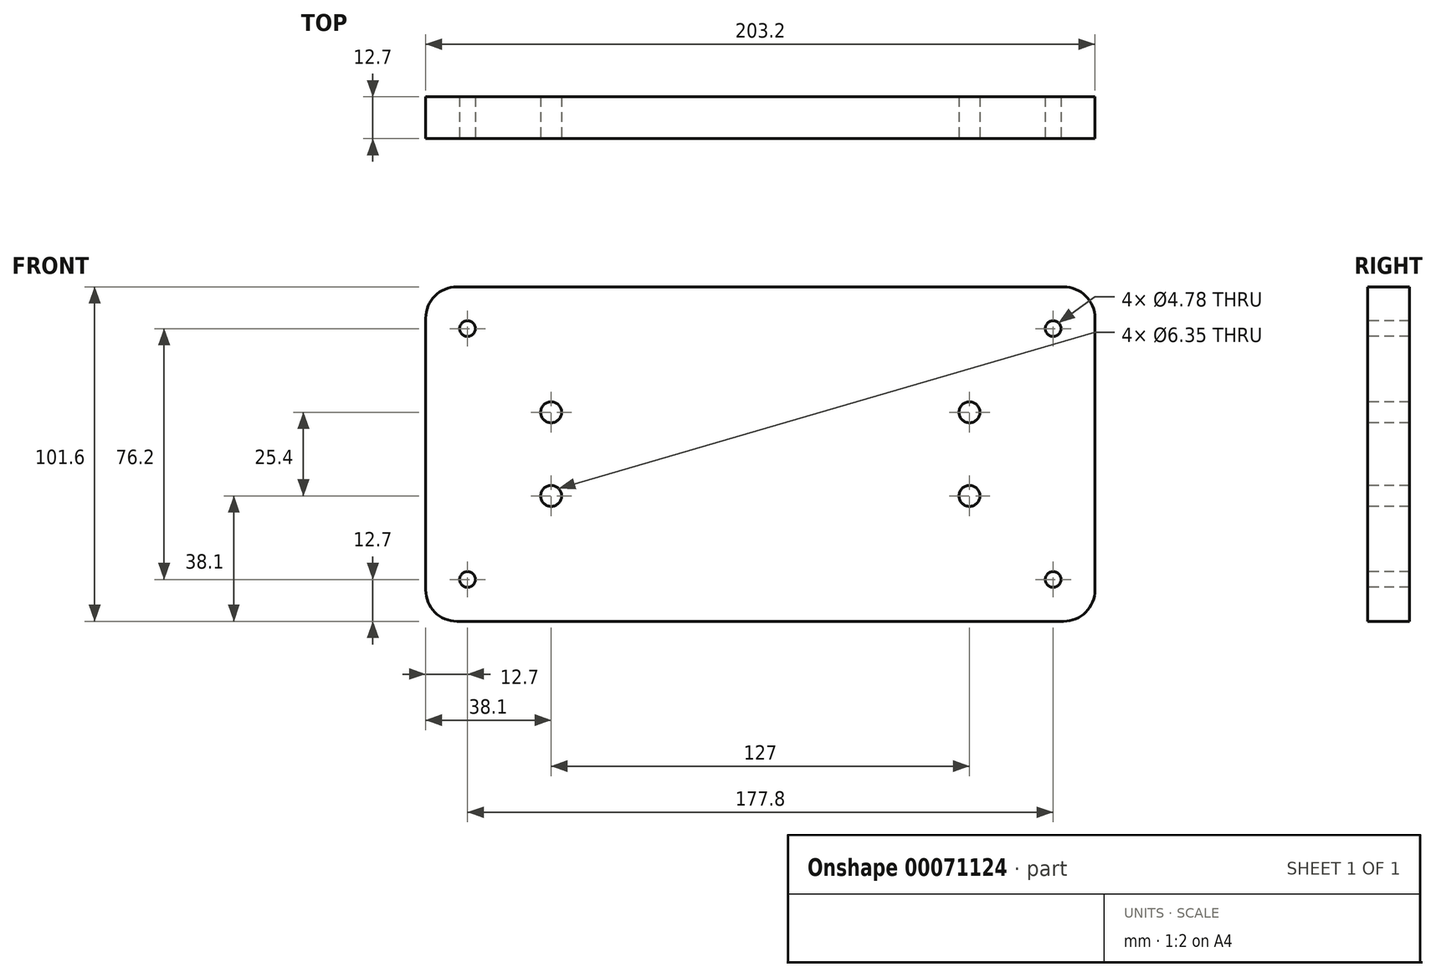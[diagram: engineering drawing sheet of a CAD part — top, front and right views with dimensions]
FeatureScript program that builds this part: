
annotation { "Feature Type Name" : "Feature", "Feature Type Description" : "" }
export const myFeature = defineFeature(function(context is Context, id is Id, definition is map)
    precondition{}
    {
        {
            var Q0;
            Q0=qCreatedBy(makeId("Front.planeOp"),FACE);
            var sketch = newSketch(context, id + "F0", { "sketchPlane" : qUnion([Q0])});
            skLineSegment(sketch, "E0.bottom", {"start": v(0, 0) * mm, "end": v(203.2, 0) * mm});
            skLineSegment(sketch, "E0.top", {"start": v(0, 101.6) * mm, "end": v(203.2, 101.6) * mm});
            skLineSegment(sketch, "E0.left", {"start": v(0, 0) * mm, "end": v(0, 101.6) * mm});
            skLineSegment(sketch, "E0.right", {"start": v(203.2, 0) * mm, "end": v(203.2, 101.6) * mm});
            skSolve(sketch);
        }
        {
            var Q0;
            Q0 = qSketchRegion(id + "F0", true);
            extrude(context, id + "F1", {"entities" : qUnion([Q0]), "depth" : 12.7 * mm});
        }
        {
            var Q0;
            Q0=makeQuery(id+"F1.opExtrude","SWEPT_EDGE",EDGE,{"disambiguationData":[OSD([sQuery(id+"F0.wireOp",EDGE,"E0.top"),sQuery(id+"F0.wireOp",EDGE,"E0.left")])]});
            var Q1;
            Q1=makeQuery(id+"F1.opExtrude","SWEPT_EDGE",EDGE,{"disambiguationData":[OSD([sQuery(id+"F0.wireOp",EDGE,"E0.bottom"),sQuery(id+"F0.wireOp",EDGE,"E0.left")])]});
            var Q2;
            Q2=makeQuery(id+"F1.opExtrude","SWEPT_EDGE",EDGE,{"disambiguationData":[OSD([sQuery(id+"F0.wireOp",EDGE,"E0.bottom"),sQuery(id+"F0.wireOp",EDGE,"E0.right")])]});
            var Q3;
            Q3=makeQuery(id+"F1.opExtrude","SWEPT_EDGE",EDGE,{"disambiguationData":[OSD([sQuery(id+"F0.wireOp",EDGE,"E0.top"),sQuery(id+"F0.wireOp",EDGE,"E0.right")])]});
            fillet(context, id + "F2", {"entities" : qUnion([Q0, Q1, Q2, Q3]), "radius" : 9.52 * mm, "tangentPropagation" : true, "allowEdgeOverflow" : false});
        }
        {
            var Q0;
            Q0=makeQuery(id+"F1.opExtrude","CAP_FACE",FACE,{"disambiguationData":[OSD([sQuery(id+"F0.wireOp",EDGE,"E0.bottom"),sQuery(id+"F0.wireOp",EDGE,"E0.top"),sQuery(id+"F0.wireOp",EDGE,"E0.left"),sQuery(id+"F0.wireOp",EDGE,"E0.right")])],"isStart":false});
            var sketch = newSketch(context, id + "F3", { "sketchPlane" : qUnion([Q0])});
            skPoint(sketch, "E1", {"position": v(12.7, 88.9) * mm});
            skPoint(sketch, "E2", {"position": v(12.7, 12.7) * mm});
            skPoint(sketch, "E3", {"position": v(190.5, 12.7) * mm});
            skPoint(sketch, "E4", {"position": v(190.5, 88.9) * mm});
            skSolve(sketch);
        }
        {
            var Q0;
            Q0=sQuery(id+"F3.wireOp",VERTEX,"E1");
            var Q1;
            Q1=sQuery(id+"F3.wireOp",VERTEX,"E2");
            var Q2;
            Q2=sQuery(id+"F3.wireOp",VERTEX,"E3");
            var Q3;
            Q3=sQuery(id+"F3.wireOp",VERTEX,"E4");
            var Q4;
            Q4=makeQuery(id+"F1.opExtrude","SWEPT_BODY",BODY,{"disambiguationData":[OSD([sQuery(id+"F0.wireOp",EDGE,"E0.bottom"),sQuery(id+"F0.wireOp",EDGE,"E0.top"),sQuery(id+"F0.wireOp",EDGE,"E0.left"),sQuery(id+"F0.wireOp",EDGE,"E0.right")])]});
            hole(context, id + "F4", {"style" : HoleStyle.SIMPLE, "holeDiameter" : 4.78 * mm, "endStyle" : HoleEndStyle.THROUGH, "locations" : qUnion([Q0, Q1, Q2, Q3]), "scope" : qUnion([Q4])});
        }
        {
            var Q0;
            Q0=makeQuery(id+"F1.opExtrude","CAP_FACE",FACE,{"disambiguationData":[OSD([sQuery(id+"F0.wireOp",EDGE,"E0.bottom"),sQuery(id+"F0.wireOp",EDGE,"E0.top"),sQuery(id+"F0.wireOp",EDGE,"E0.left"),sQuery(id+"F0.wireOp",EDGE,"E0.right")])],"isStart":false});
            var sketch = newSketch(context, id + "F5", { "sketchPlane" : qUnion([Q0])});
            skPoint(sketch, "E5", {"position": v(38.1, 63.5) * mm});
            skPoint(sketch, "E6", {"position": v(38.1, 38.1) * mm});
            skPoint(sketch, "E7", {"position": v(165.1, 63.5) * mm});
            skPoint(sketch, "E8", {"position": v(165.1, 38.1) * mm});
            skSolve(sketch);
        }
        {
            var Q0;
            Q0=sQuery(id+"F5.wireOp",VERTEX,"E5");
            var Q1;
            Q1=sQuery(id+"F5.wireOp",VERTEX,"E6");
            var Q2;
            Q2=sQuery(id+"F5.wireOp",VERTEX,"E8");
            var Q3;
            Q3=sQuery(id+"F5.wireOp",VERTEX,"E7");
            var Q4;
            Q4=makeQuery(id+"F1.opExtrude","SWEPT_BODY",BODY,{"disambiguationData":[OSD([sQuery(id+"F0.wireOp",EDGE,"E0.bottom"),sQuery(id+"F0.wireOp",EDGE,"E0.top"),sQuery(id+"F0.wireOp",EDGE,"E0.left"),sQuery(id+"F0.wireOp",EDGE,"E0.right")])]});
            hole(context, id + "F6", {"style" : HoleStyle.SIMPLE, "holeDiameter" : 6.35 * mm, "endStyle" : HoleEndStyle.THROUGH, "locations" : qUnion([Q0, Q1, Q2, Q3]), "scope" : qUnion([Q4])});
        }
    });
